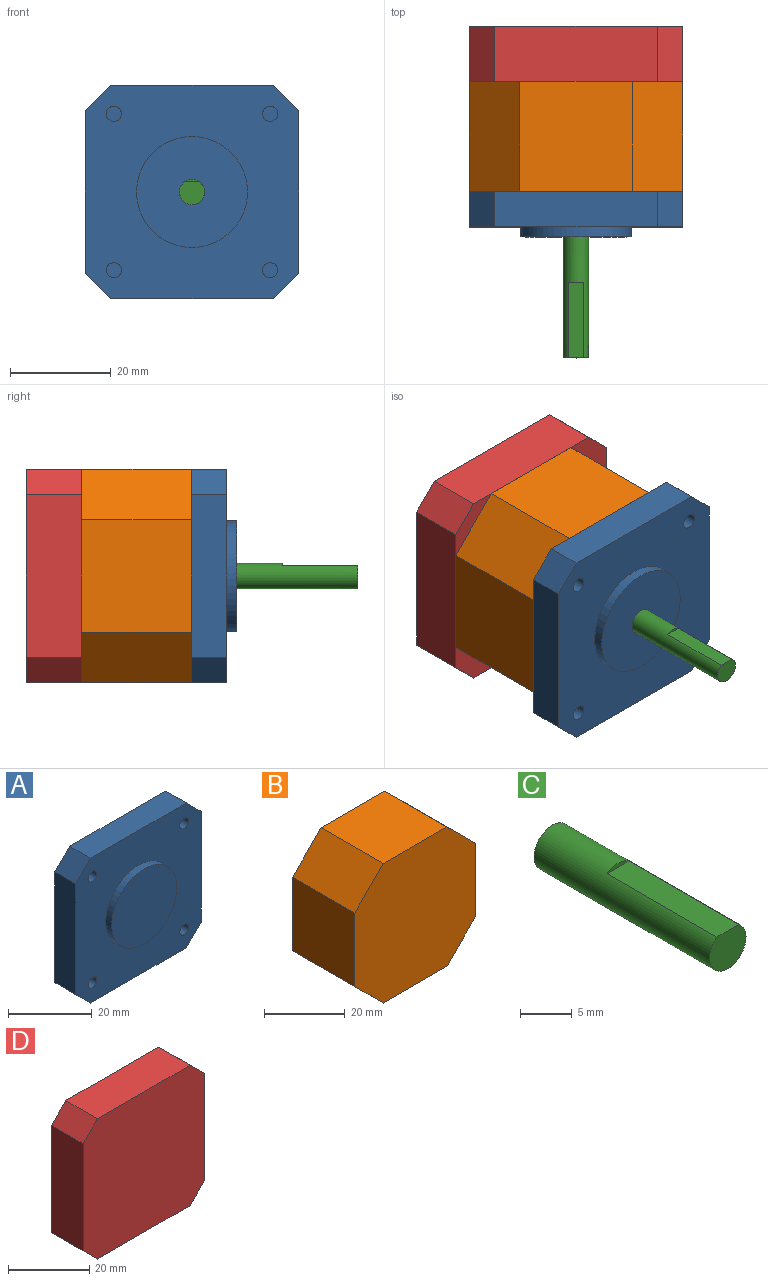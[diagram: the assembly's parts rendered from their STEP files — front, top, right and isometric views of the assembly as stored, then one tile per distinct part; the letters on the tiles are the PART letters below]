
ASSEMBLY  parts=4 mates=3
PART A: 20 faces, bbox 42.3x9x42.3 mm
  f0: plane 42.3x42.3mm, normal (0,-1,0), area 1330.9mm2, adj f1,f2,f3,f4,f6,f7,f8,f9
  f1: plane 32.3x7mm, normal (-1,0,0), area 226.1mm2, adj f0,f5,f6,f9
  f2: plane 32.3x7mm, normal (0,0,-1), area 226.1mm2, adj f0,f5,f6,f7
  f3: plane 32.3x7mm, normal (1,0,0), area 226.1mm2, adj f0,f5,f7,f8
  f4: plane 32.3x7mm, normal (0,0,1), area 226.1mm2, adj f0,f5,f8,f9
  f5: plane 42.3x42.3mm, normal (0,1,0), area 1739.3mm2, adj f1,f2,f3,f4,f6,f7,f8,f9
  f6: plane 7x5mm, normal (-0.71,0,-0.71), area 49.5mm2, adj f0,f1,f2,f5
  f7: plane 7x5mm, normal (0.71,0,-0.71), area 49.5mm2, adj f0,f2,f3,f5
  f8: plane 7x5mm, normal (0.71,0,0.71), area 49.5mm2, adj f0,f3,f4,f5
  f9: plane 7x5mm, normal (-0.71,0,0.71), area 49.5mm2, adj f0,f1,f4,f5
  f10: cylinder r=11mm len=22mm, axis (0,1,0), area 138.2mm2, adj f0,f11
  f11: plane 22x22mm, normal (0,-1,0), area 380.1mm2, adj f10
  f12: cylinder r=1.5mm len=4.5mm, axis (0,-1,0), area 42.4mm2, adj f0,f13
  f13: plane 3x3mm, normal (0,-1,0), area 7.1mm2, adj f12
  f14: cylinder r=1.5mm len=4.5mm, axis (0,-1,0), area 42.4mm2, adj f0,f15
  f15: plane 3x3mm, normal (0,-1,0), area 7.1mm2, adj f14
  f16: cylinder r=1.5mm len=4.5mm, axis (0,-1,0), area 42.4mm2, adj f0,f17
  f17: plane 3x3mm, normal (0,-1,0), area 7.1mm2, adj f16
  f18: cylinder r=1.5mm len=4.5mm, axis (0,-1,0), area 42.4mm2, adj f0,f19
  f19: plane 3x3mm, normal (0,-1,0), area 7.1mm2, adj f18
PART B: 10 faces, bbox 42.3x21.8x42.3 mm
  f0: plane 21.8x10mm, normal (0.71,0,0.71), area 308.3mm2, adj f3,f6,f7,f8
  f1: plane 21.8x10mm, normal (0.71,0,-0.71), area 308.3mm2, adj f3,f4,f6,f7
  f2: plane 21.8x10mm, normal (-0.71,0,0.71), area 308.3mm2, adj f6,f7,f8,f9
  f3: plane 22.3x21.8mm, normal (1,0,0), area 486.1mm2, adj f0,f1,f6,f7
  f4: plane 22.3x21.8mm, normal (0,0,-1), area 486.1mm2, adj f1,f5,f6,f7
  f5: plane 21.8x10mm, normal (-0.71,0,-0.71), area 308.3mm2, adj f4,f6,f7,f9
  f6: plane 42.3x42.3mm, normal (0,-1,0), area 1589.3mm2, adj f0,f1,f2,f3,f4,f5,f8,f9
  f7: plane 42.3x42.3mm, normal (0,1,0), area 1589.3mm2, adj f0,f1,f2,f3,f4,f5,f8,f9
  f8: plane 22.3x21.8mm, normal (0,0,1), area 486.1mm2, adj f0,f2,f6,f7
  f9: plane 22.3x21.8mm, normal (-1,0,0), area 486.1mm2, adj f2,f5,f6,f7
PART C: 5 faces, bbox 5x24x5 mm
  f0: cylinder r=2.5mm len=24mm, axis (0,1,0), area 328.7mm2, adj f1,f2,f3,f4
  f1: plane 5x4.5mm, normal (0,-1,0), area 18.6mm2, adj f0,f3
  f2: plane 5x5mm, normal (0,1,0), area 19.6mm2, adj f0
  f3: plane 15x3mm, normal (0,0,1), area 45mm2, adj f0,f1,f4
  f4: plane 3x0.5mm, normal (0,-1,0), area 1mm2, adj f0,f3
PART D: 18 faces, bbox 42.3x11x42.3 mm
  f0: plane 32.3x11mm, normal (1,0,0), area 355.3mm2, adj f4,f5,f8,f9
  f1: plane 32.3x11mm, normal (0,0,-1), area 355.3mm2, adj f4,f5,f7,f8
  f2: plane 32.3x11mm, normal (-1,0,0), area 355.3mm2, adj f4,f5,f6,f7
  f3: plane 32.3x11mm, normal (0,0,1), area 355.3mm2, adj f4,f5,f6,f9
  f4: plane 42.3x42.3mm, normal (0,1,0), area 1711mm2, adj f0,f1,f2,f3,f6,f7,f8,f9
  f5: plane 42.3x42.3mm, normal (0,-1,0), area 1739.3mm2, adj f0,f1,f2,f3,f6,f7,f8,f9
  f6: plane 11x5mm, normal (-0.71,0,0.71), area 77.8mm2, adj f2,f3,f4,f5
  f7: plane 11x5mm, normal (-0.71,0,-0.71), area 77.8mm2, adj f1,f2,f4,f5
  f8: plane 11x5mm, normal (0.71,0,-0.71), area 77.8mm2, adj f0,f1,f4,f5
  f9: plane 11x5mm, normal (0.71,0,0.71), area 77.8mm2, adj f0,f3,f4,f5
  f10: cylinder r=1.5mm len=4.5mm, axis (0,1,0), area 42.4mm2, adj f4,f11
  f11: plane 3x3mm, normal (0,1,0), area 7.1mm2, adj f10
  f12: cylinder r=1.5mm len=4.5mm, axis (0,1,0), area 42.4mm2, adj f4,f13
  f13: plane 3x3mm, normal (0,1,0), area 7.1mm2, adj f12
  f14: cylinder r=1.5mm len=4.5mm, axis (0,1,0), area 42.4mm2, adj f4,f15
  f15: plane 3x3mm, normal (0,1,0), area 7.1mm2, adj f14
  f16: cylinder r=1.5mm len=4.5mm, axis (0,1,0), area 42.4mm2, adj f4,f17
  f17: plane 3x3mm, normal (0,1,0), area 7.1mm2, adj f16
PLACE A t=(0,8.46,76.23)mm
PLACE B t=(0,8.46,76.23)mm
PLACE C t=(0,8.46,76.23)mm
PLACE D t=(0,8.46,76.23)mm
MATE revolute C.f0 <-> A.f10  axis (0,1,0) through (-18.45,-0.54,89.66)mm
MATE fastened A.f10 <-> B.f6  axis (0,1,0) through (-18.45,8.46,89.66)mm
MATE fastened B.f7 <-> D.f5  axis (0,1,0) through (-18.45,30.26,89.66)mm
